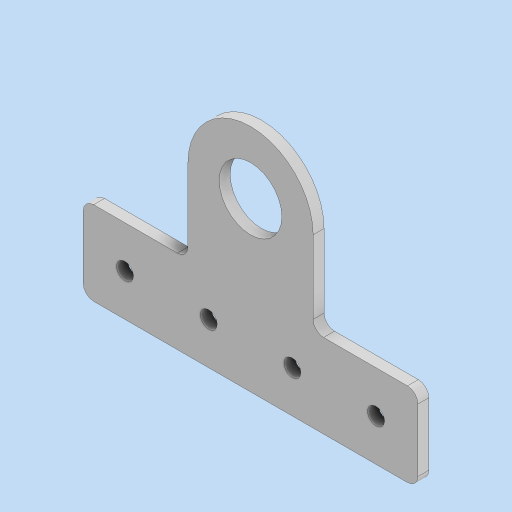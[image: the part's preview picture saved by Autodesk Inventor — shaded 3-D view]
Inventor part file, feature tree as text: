
AUTODESK INVENTOR PART (.ipt)
format: ipt  version: 2024 (Build 280153000, 153)  size: 142,336 bytes
history: native  units: in
note: dims shown in document units (in); Inventor stores cm internally (conversion verified against a paired STEP export)
features: extrude x1, fillet x1, sketch x1
ambient origin geometry x8: Origin, YZ Plane, XZ Plane, XY Plane, X Axis, Y Axis, Z Axis, Center Point
bodies: Solid1 (feature_tree)
feature tree (3):
  extrude  "Extrusion1"  Depth=0.748in
  fillet  "Fillet1"  Radius=0.13in
  sketch  "Sketch1"  dims[d0=1.4961in d1=0.748in d8=0.13in d9=0.0in d10=0.203in d11=0.203in d12=0.5in d13=0.5in d14=0.5in d15=0.5in d16=2.0in d17=1.0in d18=4.0in d19=2.0in d20=1.0in d21=1.0in d22=0.125in]
